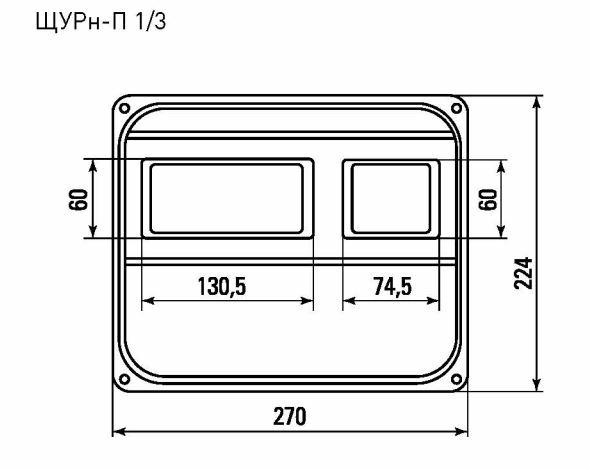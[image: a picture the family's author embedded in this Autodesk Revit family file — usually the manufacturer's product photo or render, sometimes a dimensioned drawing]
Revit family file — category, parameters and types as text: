
# Revit family: EKF_EE_Короб_Верхний_КСС-КЭТ(600х300х150)_Basic
name_source: partatom
category: Электрооборудование
units: mm (PartAtom-declared; Revit-internal decimal feet)

## family parameters
Всегда вертикально = Да
На основе рабочей плоскости = Нет
Общий = Нет
При загрузке вырезать с полостями = Нет
Размер круглого соединителя = Использовать диаметр
Тип детали = Силовой щит
Точка расчета площади = Да

## types (1)
- Короб верхний для КСС/КЭТ (600х300х150) EKF Basic
    ADSK_Единица измерения = компл.
    ADSK_Завод-изготовитель = EKF
    ADSK_Классификация нагрузок = Прочее
    ADSK_Код изделия = uerm-kor-600
    ADSK_Количество = 1
    ADSK_Количество фаз = 3
    ADSK_Коэффициент мощности = 1
    ADSK_Марка = Короб верхний для КСС/КЭТ
    ADSK_Масса = 0
    ADSK_Материал = RAL 7035_Сталь
    ADSK_Наименование = Короб верхний для КСС/КЭТ (600х300х150) EKF BasicКороб верхний для КСС/КЭТ (600х300х150) EKF Basic
    ADSK_Напряжение = 400 В
    ADSK_Номинальная мощность = 0 Вт
    ADSK_Обозначение = Короб верхний для КСС/КЭТ
    ADSK_Полная мощность = 0 В·А
    ADSK_Размер_Высота = 600 мм
    ADSK_Размер_Глубина = 150 мм
    ADSK_Размер_Ширина = 300 мм
    ADSK_Ток = 125 А
    Изготовитель = EKF
    Количество DIN-реек = 0
    Количество модулей на DIN-рейке = 0
    Максимальное количество модулей = 0
    Описание = Короб верхний для КСС/КЭТ (600х300х150) EKF BasicКороб верхний для КСС/КЭТ (600х300х150) EKF Basic
    Серия номенклатуры = Basic
    Степень защиты IP = IP31
    ТВ = EKF
    Тип = 205 мм
    Тип установки = Навесной
